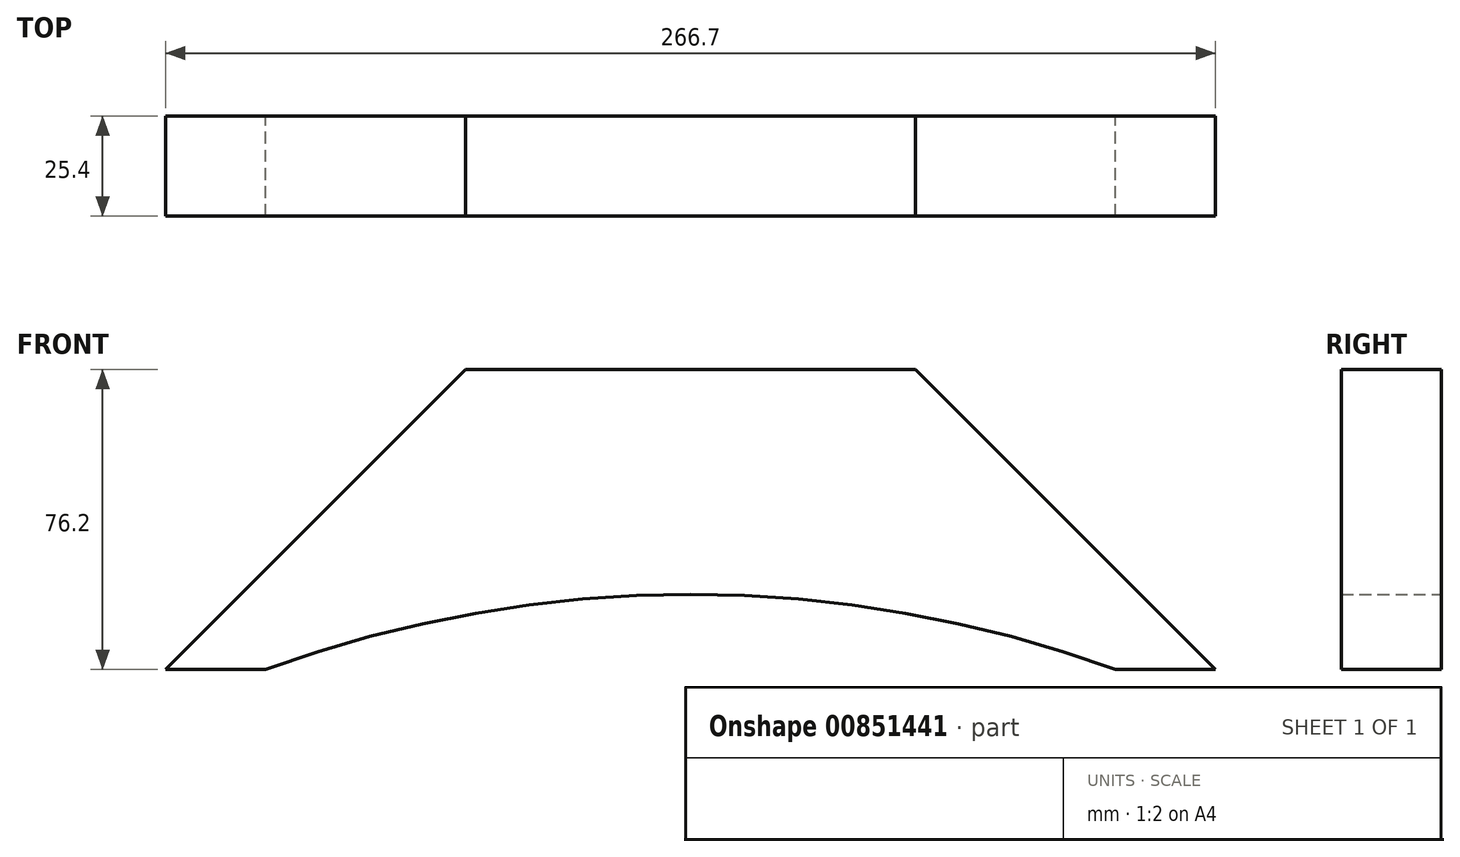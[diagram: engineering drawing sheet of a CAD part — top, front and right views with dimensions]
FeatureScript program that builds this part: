
annotation { "Feature Type Name" : "Feature", "Feature Type Description" : "" }
export const myFeature = defineFeature(function(context is Context, id is Id, definition is map)
    precondition{}
    {
        {
            var Q0;
            Q0=qCreatedBy(makeId("Front.planeOp"),FACE);
            var sketch = newSketch(context, id + "F0", { "sketchPlane" : qUnion([Q0])});
            skLineSegment(sketch, "E0", {"start": v(0, 0) * mm, "end": v(25.4, 0) * mm});
            skLineSegment(sketch, "E1", {"start": v(25.4, 0) * mm, "end": v(-50.8, 76.2) * mm});
            skLineSegment(sketch, "E2", {"start": v(-50.8, 76.2) * mm, "end": v(-165.1, 76.2) * mm});
            skLineSegment(sketch, "E3", {"start": v(-165.1, 76.2) * mm, "end": v(-241.3, 0) * mm});
            skLineSegment(sketch, "E4", {"start": v(-241.3, 0) * mm, "end": v(-215.9, 0) * mm});
            skLineSegment(sketch, "E5", {"start": v(-50.8, 76.2) * mm, "end": v(43.9, 76.2) * mm, "construction": true});
            skLineSegment(sketch, "E6", {"start": v(-136.67, 76.2) * mm, "end": v(-165.1, 76.2) * mm, "construction": true});
            skArc(sketch, "E7", {"start": v(0, 0) * mm, "mid": v(-107.95, 19.05) * mm, "end": v(-215.9, 0) * mm});
            skPoint(sketch, "E8", {"position": v(-107.95, 19.05) * mm});
            skSolve(sketch);
        }
        {
            var Q0;
            Q0 = qSketchRegion(id + "F0", true);
            extrude(context, id + "F1", {"entities" : qUnion([Q0]), "depth" : 25.4 * mm, "offsetDistance" : 25.4 * mm});
        }
    });
